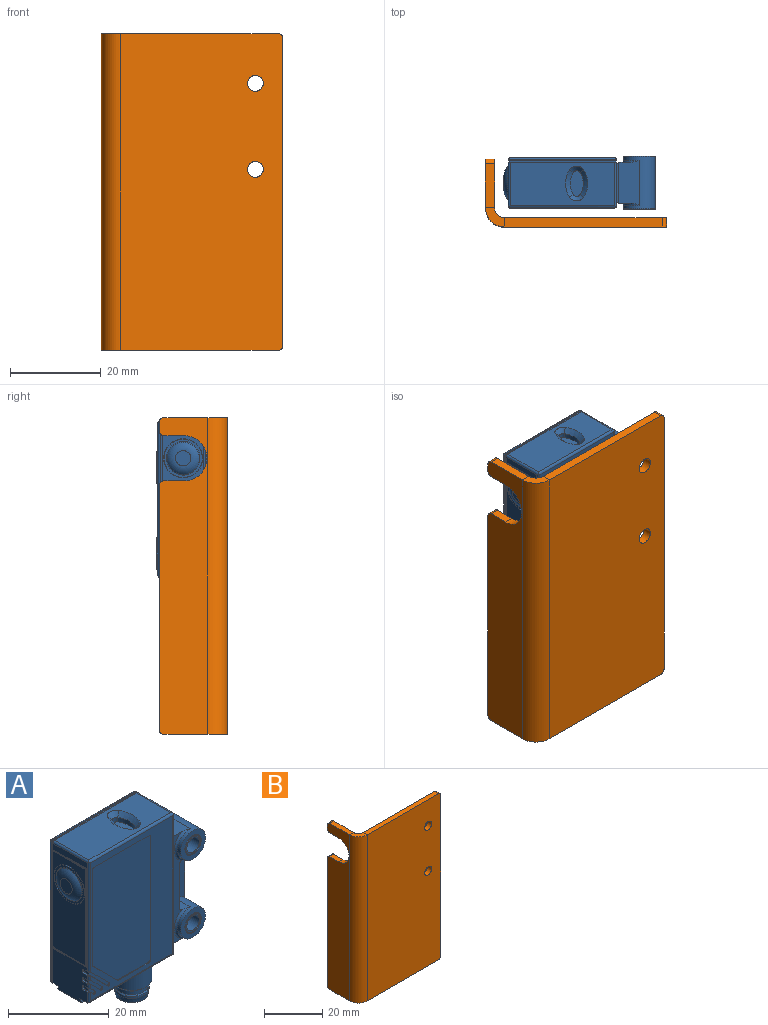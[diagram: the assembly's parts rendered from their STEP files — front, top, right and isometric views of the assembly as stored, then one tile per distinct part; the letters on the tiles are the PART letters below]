
ASSEMBLY  parts=2 mates=1
PART A: 180 faces, bbox 33.5x12.5x43.6 mm
  f0: cylinder r=4mm len=8mm, axis (0,0,-1), area 110.2mm2, adj f1,f8
  f1: cone r=3.69mm half-angle=45deg, axis (0,0,1), area 20.1mm2, adj f0,f179
  f2: cylinder r=3.25mm len=6.5mm, axis (0,0,-1), area 20.4mm2, adj f3,f179
  f3: cone r=3.35mm half-angle=38.7deg, axis (0,0,-1), area 6.7mm2, adj f2,f4
  f4: cylinder r=3.45mm len=6.9mm, axis (0,0,-1), area 10.8mm2, adj f3,f5
  f5: cone r=3.36mm half-angle=9.1deg, axis (0,0,1), area 23.1mm2, adj f4,f6
  f6: torus R=3.08mm, axis (0,0,1), area 5.7mm2, adj f5,f178
  f7: cylinder r=2.9mm len=5.8mm, axis (0,0,-1), area 91.1mm2, adj f177,f178
  f8: torus R=5mm, axis (0,0,1), area 40.8mm2, adj f0,f121,f170,f171
  f9: torus R=4mm, axis (0,-1,0), area 7.6mm2, adj f14,f98,f105,f107
  f10: torus R=4mm, axis (0,-1,0), area 7.6mm2, adj f13,f91,f101,f107
  f11: torus R=4mm, axis (0,-1,0), area 7.6mm2, adj f14,f100,f102,f105
  f12: torus R=4mm, axis (0,-1,0), area 7.6mm2, adj f13,f92,f101,f102
  f13: cylinder r=3.5mm len=11.6mm, axis (0,1,0), area 140.1mm2, adj f10,f12,f79,f84,f85,f87,f89,f90
  f14: cylinder r=3.5mm len=11.6mm, axis (0,1,0), area 140.1mm2, adj f9,f11,f82,f84,f85,f87,f89,f90
  f15: cone r=2.25mm half-angle=45deg, axis (0,-1,0), area 2mm2, adj f16,f82
  f16: cone r=2.12mm half-angle=56.3deg, axis (0,1,0), area 2.4mm2, adj f15,f83
  f17: cylinder r=1.75mm len=11.6mm, axis (0,1,0), area 127.5mm2, adj f81,f83
  f18: cone r=2.12mm half-angle=56.3deg, axis (0,-1,0), area 2.4mm2, adj f19,f81
  f19: cone r=2.25mm half-angle=45deg, axis (0,1,0), area 2mm2, adj f18,f104
  f20: cone r=2.25mm half-angle=45deg, axis (0,-1,0), area 2mm2, adj f21,f79
  f21: cone r=2.12mm half-angle=56.3deg, axis (0,1,0), area 2.4mm2, adj f20,f80
  f22: cylinder r=1.75mm len=11.6mm, axis (0,1,0), area 127.5mm2, adj f78,f80
  f23: cone r=2.12mm half-angle=56.3deg, axis (0,-1,0), area 2.4mm2, adj f24,f78
  f24: cone r=2.25mm half-angle=45deg, axis (0,1,0), area 2mm2, adj f23,f103
  f25: torus R=1.7mm, axis (-1,0,0), area 35.5mm2, adj f26,f53
  f26: torus R=3.71mm, axis (-1,0,0), area 3.8mm2, adj f25,f52
  f27: cylinder r=4.23mm len=8.45mm, axis (1,0,0), area 0.3mm2, adj f51,f52
  f28: cylinder r=4.3mm len=8.6mm, axis (1,0,0), area 118.9mm2, adj f50,f68
  f29: cylinder r=4.22mm len=8.45mm, axis (1,0,0), area 116.8mm2, adj f50,f51
  f30: plane 1.39x0.4mm, normal (0,0,1), area 0.5mm2, adj f34,f37,f48,f49
  f31: plane 1.39x0.4mm, normal (0,0,1), area 0.5mm2, adj f32,f39,f46,f49
  f32: plane 1.89x0.99mm, normal (-1,0,0), area 1.4mm2, adj f31,f38,f39,f43,f46,f136
  f33: plane 1.89x0.99mm, normal (-1,0,0), area 1.4mm2, adj f35,f40,f41,f44,f45,f138
  f34: plane 1.89x0.99mm, normal (-1,0,0), area 1.4mm2, adj f30,f36,f37,f42,f48,f146
  f35: plane 1.39x0.4mm, normal (0,0,1), area 0.5mm2, adj f33,f41,f45,f49
  f36: plane 1x0.4mm, normal (0,0,-1), area 0.4mm2, adj f34,f37,f47,f49,f154
  f37: cylinder r=0.49mm len=0.99mm, axis (-1,0,0), area 0.6mm2, adj f30,f34,f36,f49
  f38: plane 1x0.4mm, normal (0,0,-1), area 0.4mm2, adj f32,f39,f48,f49,f151
  f39: cylinder r=0.49mm len=0.99mm, axis (-1,0,0), area 0.6mm2, adj f31,f32,f38,f49
  f40: plane 1x0.4mm, normal (0,0,-1), area 0.4mm2, adj f33,f41,f46,f49,f137
  f41: cylinder r=0.49mm len=0.99mm, axis (-1,0,0), area 0.6mm2, adj f33,f35,f40,f49
  f42: plane 4.91x4.91mm, normal (0.71,0,0.71), area 2.8mm2, adj f34,f48,f146,f152,f172
  f43: plane 2.91x2.91mm, normal (0.71,0,0.71), area 1.6mm2, adj f32,f46,f136,f149,f172
  f44: plane 0.91x0.91mm, normal (0.71,0,0.71), area 0.5mm2, adj f33,f45,f138,f147,f172
  f45: cylinder r=0.5mm len=2.61mm, axis (0,0,-1), area 1.9mm2, adj f33,f35,f44,f49,f168,f172
  f46: cylinder r=0.5mm len=1.11mm, axis (0,0,-1), area 0.8mm2, adj f31,f32,f40,f43,f49,f137,f148,f172
  f47: cylinder r=0.5mm len=26.85mm, axis (0,0,-1), area 20.9mm2, adj f36,f49,f139,f140,f153,f154,f172
  f48: cylinder r=0.5mm len=1.11mm, axis (0,0,-1), area 0.8mm2, adj f30,f34,f38,f42,f49,f150,f151,f172
  f49: plane 34.82x9.6mm, normal (-1,0,0), area 99.8mm2, adj f30,f31,f35,f36,f37,f38,f39,f40
  f50: plane 8.6x8.6mm, normal (-1,0,0), area 2mm2, adj f28,f29
  f51: plane 8.45x8.45mm, normal (1,0,0), area 0mm2, adj f27,f29
  f52: plane 8.45x8.45mm, normal (-1,0,0), area 12.8mm2, adj f26,f27
  f53: plane 3.4x3.4mm, normal (-1,0,0), area 9.1mm2, adj f25
  f54: plane 9.3x0.2mm, normal (0,0,-1), area 1.9mm2, adj f49,f62,f67,f162
  f55: cylinder r=0.2mm len=0.2mm, axis (-1,0,0), area 0.1mm2, adj f56,f61,f68,f162
  f56: plane 8.8x0.2mm, normal (0,0,-1), area 1.8mm2, adj f55,f57,f68,f162
  f57: cylinder r=0.2mm len=0.2mm, axis (-1,0,0), area 0.1mm2, adj f56,f66,f68,f162
  f58: cylinder r=0.2mm len=0.2mm, axis (-1,0,0), area 0.1mm2, adj f59,f66,f68,f162
  f59: plane 8.8x0.2mm, normal (0,0,1), area 1.8mm2, adj f58,f60,f68,f162
  f60: cylinder r=0.2mm len=0.2mm, axis (-1,0,0), area 0.1mm2, adj f59,f61,f68,f162
  f61: plane 23x0.2mm, normal (0,-1,0), area 4.6mm2, adj f55,f60,f68,f162
  f62: cylinder r=0.2mm len=0.2mm, axis (-1,0,0), area 0.1mm2, adj f49,f54,f65,f162
  f63: plane 9.3x0.2mm, normal (0,0,1), area 1.9mm2, adj f49,f64,f67,f162
  f64: cylinder r=0.2mm len=0.2mm, axis (-1,0,0), area 0.1mm2, adj f49,f63,f65,f162
  f65: plane 23.6x0.2mm, normal (0,1,0), area 4.7mm2, adj f49,f62,f64,f162
  f66: plane 23x0.2mm, normal (0,1,0), area 4.6mm2, adj f57,f58,f68,f162
  f67: plane 34.5x24mm, normal (0,1,0), area 18.4mm2, adj f49,f54,f63,f121,f139,f141,f142,f155
  f68: plane 23.4x9.2mm, normal (-1,0,0), area 157.2mm2, adj f28,f55,f56,f57,f58,f59,f60,f61
  f69: cylinder r=0.88mm len=1.49mm, axis (0,0,1), area 2mm2, adj f70,f72,f73,f74
  f70: cylinder r=4.53mm len=4.88mm, axis (0,0,1), area 5.7mm2, adj f69,f71,f73,f77
  f71: cylinder r=0.88mm len=1.49mm, axis (0,0,1), area 2mm2, adj f70,f72,f73,f76
  f72: cylinder r=4.63mm len=4.85mm, axis (0,0,1), area 5.6mm2, adj f69,f71,f73,f75
  f73: plane 5.69x2.89mm, normal (0,0,1), area 12.7mm2, adj f69,f70,f71,f72
  f74: cone r=0.88mm half-angle=45deg, axis (0,0,1), area 3.9mm2, adj f69,f75,f77,f167
  f75: cone r=4.63mm half-angle=45deg, axis (0,0,1), area 8mm2, adj f72,f74,f76,f167
  f76: cone r=0.88mm half-angle=45deg, axis (0,0,1), area 3.9mm2, adj f71,f75,f77,f167
  f77: cone r=4.53mm half-angle=45deg, axis (0,0,1), area 8.1mm2, adj f70,f74,f76,f167
  f78: plane 4.1x4.1mm, normal (0,1,0), area 3.6mm2, adj f22,f23
  f79: plane 7x7mm, normal (0,-1,0), area 21.9mm2, adj f13,f20
  f80: plane 4.1x4.1mm, normal (0,-1,0), area 3.6mm2, adj f21,f22
  f81: plane 4.1x4.1mm, normal (0,1,0), area 3.6mm2, adj f17,f18
  f82: plane 7x7mm, normal (0,-1,0), area 21.9mm2, adj f14,f15
  f83: plane 4.1x4.1mm, normal (0,-1,0), area 3.6mm2, adj f16,f17
  f84: plane 15.39x0.5mm, normal (1,0,0), area 7.7mm2, adj f13,f14,f85,f90
  f85: cylinder r=0.5mm len=15.39mm, axis (0,0,-1), area 11.6mm2, adj f13,f14,f84,f87
  f86: cylinder r=0.5mm len=12mm, axis (0,0,-1), area 9mm2, adj f87,f93,f95,f97
  f87: plane 14.1x4.5mm, normal (0,-1,0), area 55.6mm2, adj f13,f14,f85,f86,f91,f98
  f88: cylinder r=0.5mm len=12mm, axis (0,0,-1), area 9mm2, adj f89,f94,f96,f99
  f89: plane 14.1x4.5mm, normal (0,1,0), area 55.6mm2, adj f13,f14,f88,f90,f92,f100
  f90: cylinder r=0.5mm len=15.39mm, axis (0,0,-1), area 11.6mm2, adj f13,f14,f84,f89
  f91: plane 4.34x2.14mm, normal (0,0,-1), area 7.8mm2, adj f10,f13,f87,f93,f107
  f92: plane 4.44x2.14mm, normal (0,0,-1), area 8mm2, adj f12,f13,f89,f94,f102
  f93: cylinder r=0.5mm len=3.7mm, axis (0,-1,0), area 2.7mm2, adj f86,f91,f95,f107
  f94: cylinder r=0.5mm len=3.8mm, axis (0,-1,0), area 2.8mm2, adj f88,f92,f96,f102
  f95: plane 11x3.2mm, normal (1,0,0), area 35.2mm2, adj f86,f93,f97,f107
  f96: plane 11x3.3mm, normal (1,0,0), area 36.3mm2, adj f88,f94,f99,f102
  f97: cylinder r=0.5mm len=3.7mm, axis (0,-1,0), area 2.7mm2, adj f86,f95,f98,f107
  f98: plane 4.34x2.14mm, normal (0,0,1), area 7.8mm2, adj f9,f14,f87,f97,f107
  f99: cylinder r=0.5mm len=3.8mm, axis (0,-1,0), area 2.8mm2, adj f88,f96,f100,f102
  f100: plane 4.44x2.14mm, normal (0,0,1), area 8mm2, adj f11,f14,f89,f99,f102
  f101: plane 10.14x4.69mm, normal (0,0,1), area 41.7mm2, adj f10,f12,f13,f102,f106,f107
  f102: plane 26x2.61mm, normal (0,1,0), area 40.8mm2, adj f11,f12,f92,f94,f96,f99,f100,f101
  f103: plane 7x7mm, normal (0,1,0), area 21.9mm2, adj f13,f24
  f104: plane 7x7mm, normal (0,1,0), area 21.9mm2, adj f14,f19
  f105: plane 10.14x4.69mm, normal (0,0,-1), area 41.7mm2, adj f9,f11,f14,f102,f106,f107
  f106: plane 26x9mm, normal (-1,0,0), area 13.8mm2, adj f101,f102,f105,f107,f108,f109,f110,f111
  f107: plane 26x2.61mm, normal (0,-1,0), area 40.8mm2, adj f9,f10,f91,f93,f95,f97,f98,f101
  f108: plane 25.6x0.45mm, normal (0,-1,0), area 11.5mm2, adj f106,f109,f111,f142
  f109: plane 8.6x0.45mm, normal (0,0,1), area 3.9mm2, adj f106,f108,f110,f142
  f110: plane 25.6x0.45mm, normal (0,1,0), area 11.5mm2, adj f106,f109,f111,f142
  f111: plane 8.6x0.45mm, normal (0,0,-1), area 3.9mm2, adj f106,f108,f110,f142
  f112: plane 3.8x1.64mm, normal (-0.45,0,-0.89), area 7mm2, adj f113,f114,f116,f119
  f113: plane 2.33x0.82mm, normal (0,-1,0), area 1.1mm2, adj f112,f114,f115,f119
  f114: plane 3.8x0.3mm, normal (0,0,-1), area 1.1mm2, adj f112,f113,f115,f116
  f115: plane 3.8x0.82mm, normal (0.91,0,-0.42), area 3.4mm2, adj f113,f114,f116,f119
  f116: plane 2.33x0.82mm, normal (0,1,0), area 1.1mm2, adj f112,f114,f115,f119
  f117: plane 11.9x0.82mm, normal (0,-0.88,0.47), area 11.1mm2, adj f49,f119,f120,f121
  f118: plane 11.9x0.82mm, normal (0,0.88,0.47), area 11.1mm2, adj f49,f119,f120,f121
  f119: plane 11.9x6.77mm, normal (0,0,-1), area 71.7mm2, adj f49,f112,f113,f115,f116,f117,f118,f120
  f120: plane 6.77x0.82mm, normal (1,0,0), area 5.2mm2, adj f117,f118,f119,f121
  f121: plane 23.5x9.6mm, normal (0,0,-1), area 79.1mm2, adj f8,f49,f67,f117,f118,f120,f164,f168
  f122: plane 6.92x6.92mm, normal (0.71,0,0.71), area 2mm2, adj f123,f131,f132,f172
  f123: cylinder r=0.3mm len=0.21mm, axis (0,-1,0), area 0mm2, adj f122,f124,f132,f172
  f124: plane 8.68x0.2mm, normal (0,0,1), area 1.7mm2, adj f123,f125,f132,f172
  f125: cylinder r=0.5mm len=0.5mm, axis (0,-1,0), area 0.2mm2, adj f124,f126,f132,f172
  f126: plane 29.9x0.2mm, normal (-1,0,0), area 6mm2, adj f125,f127,f132,f172
  f127: cylinder r=0.5mm len=0.5mm, axis (0,-1,0), area 0.2mm2, adj f126,f128,f132,f172
  f128: plane 15.4x0.2mm, normal (0,0,-1), area 3.1mm2, adj f127,f129,f132,f172
  f129: cylinder r=0.5mm len=0.5mm, axis (0,-1,0), area 0.2mm2, adj f128,f130,f132,f172
  f130: plane 23.18x0.2mm, normal (1,0,0), area 4.6mm2, adj f129,f131,f132,f172
  f131: cylinder r=0.3mm len=0.21mm, axis (0,-1,0), area 0mm2, adj f122,f130,f132,f172
  f132: plane 30.9x16.4mm, normal (0,-1,0), area 481.4mm2, adj f122,f123,f124,f125,f126,f127,f128,f129
  f133: cylinder r=0.5mm len=34.21mm, axis (0,0,-1), area 26.6mm2, adj f140,f141,f142,f164,f168,f172
  f134: cylinder r=0.5mm len=34.21mm, axis (0,0,-1), area 26.6mm2, adj f144,f145,f169,f174,f175,f176
  f135: cylinder r=0.5mm len=34.35mm, axis (0,0,-1), area 26.6mm2, adj f143,f145,f166,f169,f174
  f136: plane 3.99x3.5mm, normal (0,-1,0), area 3.3mm2, adj f32,f43,f149,f150,f151
  f137: plane 0.4x0.39mm, normal (0,0,-1), area 0.1mm2, adj f40,f46,f138,f148
  f138: plane 1.99x1.5mm, normal (0,-1,0), area 1.3mm2, adj f33,f44,f137,f147,f148
  f139: cylinder r=0.5mm len=9.95mm, axis (0,1,0), area 7.7mm2, adj f47,f49,f67,f140,f167
  f140: cylinder r=0.5mm len=23.71mm, axis (-1,0,0), area 18.3mm2, adj f47,f133,f139,f141,f167,f172
  f141: cylinder r=0.5mm len=9.95mm, axis (0,1,0), area 7.7mm2, adj f67,f133,f140,f142,f167
  f142: plane 33.5x9.6mm, normal (1,0,0), area 101.4mm2, adj f67,f108,f109,f110,f111,f133,f141,f164
  f143: plane 34x0.1mm, normal (-1,0,0), area 3.4mm2, adj f135,f163,f165,f166
  f144: cylinder r=0.5mm len=0.5mm, axis (0,1,0), area 0.2mm2, adj f134,f163,f169,f173,f175
  f145: cylinder r=0.5mm len=23.85mm, axis (-1,0,0), area 18.4mm2, adj f134,f135,f165,f174,f176
  f146: plane 5.99x5.5mm, normal (0,-1,0), area 5.3mm2, adj f34,f42,f152,f153,f154
  f147: cylinder r=0.35mm len=0.6mm, axis (0,-1,0), area 0.4mm2, adj f44,f138,f148,f172
  f148: plane 1.39x1.39mm, normal (-0.71,0,-0.71), area 0.8mm2, adj f46,f137,f138,f147,f172
  f149: cylinder r=0.35mm len=0.6mm, axis (0,-1,0), area 0.4mm2, adj f43,f136,f150,f172
  f150: plane 3.39x3.39mm, normal (-0.71,0,-0.71), area 1.9mm2, adj f48,f136,f149,f151,f172
  f151: plane 0.4x0.39mm, normal (0,0,-1), area 0.1mm2, adj f38,f48,f136,f150
  f152: cylinder r=0.35mm len=0.6mm, axis (0,-1,0), area 0.4mm2, adj f42,f146,f153,f172
  f153: plane 5.39x5.39mm, normal (-0.71,0,-0.71), area 3.1mm2, adj f47,f146,f152,f154,f172
  f154: plane 0.4x0.39mm, normal (0,0,-1), area 0.1mm2, adj f36,f47,f146,f153
  f155: cylinder r=0.3mm len=0.4mm, axis (0,-1,0), area 0.2mm2, adj f67,f156,f162,f163
  f156: plane 23x0.4mm, normal (0,0,1), area 9.2mm2, adj f67,f155,f157,f163
  f157: cylinder r=0.3mm len=0.4mm, axis (0,-1,0), area 0.2mm2, adj f67,f156,f158,f163
  f158: plane 33.5x0.4mm, normal (1,0,0), area 13.4mm2, adj f67,f157,f159,f163
  f159: cylinder r=0.3mm len=0.4mm, axis (0,-1,0), area 0.2mm2, adj f67,f158,f160,f163
  f160: plane 23x0.4mm, normal (0,0,-1), area 9.2mm2, adj f67,f159,f161,f163
  f161: cylinder r=0.3mm len=0.4mm, axis (0,-1,0), area 0.2mm2, adj f67,f160,f162,f163
  f162: plane 33.5x9.9mm, normal (-1,0,0), area 26.1mm2, adj f54,f55,f56,f57,f58,f59,f60,f61
  f163: plane 34.5x24mm, normal (0,-1,0), area 23.2mm2, adj f143,f144,f155,f156,f157,f158,f159,f160
  f164: cylinder r=0.5mm len=9.95mm, axis (0,1,0), area 7.7mm2, adj f67,f121,f133,f142,f168
  f165: plane 23.5x0.1mm, normal (0,0,-1), area 2.4mm2, adj f143,f145,f163,f176
  f166: cylinder r=0.5mm len=0.5mm, axis (0,1,0), area 0.2mm2, adj f135,f143,f163,f169,f173
  f167: plane 23x9.6mm, normal (0,0,1), area 191.1mm2, adj f67,f74,f75,f76,f77,f139,f140,f141
  f168: cylinder r=0.5mm len=23.85mm, axis (-1,0,0), area 18.4mm2, adj f45,f121,f133,f164,f172
  f169: cylinder r=0.5mm len=23.71mm, axis (-1,0,0), area 18.3mm2, adj f134,f135,f144,f166,f173,f174
  f170: cylinder r=2mm len=3.92mm, axis (-1,0,0), area 0.4mm2, adj f8,f121
  f171: cylinder r=2mm len=3.92mm, axis (-1,0,0), area 0.4mm2, adj f8,f121
  f172: plane 33.5x23mm, normal (0,-1,0), area 279.5mm2, adj f42,f43,f44,f45,f46,f47,f48,f122
  f173: plane 23x0.1mm, normal (0,0,1), area 2.3mm2, adj f144,f163,f166,f169
  f174: plane 33.5x23mm, normal (0,1,0), area 770.5mm2, adj f134,f135,f145,f169
  f175: plane 33.5x0.1mm, normal (1,0,0), area 3.4mm2, adj f134,f144,f163,f176
  f176: cylinder r=0.5mm len=0.5mm, axis (0,1,0), area 0.2mm2, adj f134,f145,f163,f165,f175
  f177: plane 5.8x5.8mm, normal (0,0,-1), area 26.4mm2, adj f7
  f178: plane 6.16x6.16mm, normal (0,0,-1), area 3.4mm2, adj f6,f7
  f179: plane 6.77x6.77mm, normal (0,0,-1), area 2.8mm2, adj f1,f2
PART B: 26 faces, bbox 40x15x70 mm
  f0: plane 34.7x2mm, normal (0,0,1), area 69.4mm2, adj f5,f6,f8,f23
  f1: plane 68x2mm, normal (1,0,0), area 136mm2, adj f5,f6,f7,f8
  f2: cylinder r=1.75mm len=3.5mm, axis (0,-1,0), area 22mm2, adj f5,f6
  f3: cylinder r=1.75mm len=3.5mm, axis (0,-1,0), area 22mm2, adj f5,f6
  f4: plane 34.7x2mm, normal (0,0,-1), area 69.4mm2, adj f5,f6,f7,f22
  f5: plane 70x35.7mm, normal (0,1,0), area 2479.3mm2, adj f0,f1,f2,f3,f4,f7,f8,f25
  f6: plane 70x35.7mm, normal (0,-1,0), area 2479.3mm2, adj f0,f1,f2,f3,f4,f7,f8,f24
  f7: cylinder r=1mm len=2mm, axis (0,-1,0), area 3.1mm2, adj f1,f4,f5,f6
  f8: cylinder r=1mm len=2mm, axis (0,-1,0), area 3.1mm2, adj f0,f1,f5,f6
  f9: plane 2x2mm, normal (0,1,0), area 4mm2, adj f16,f17,f19,f21
  f10: plane 9.7x2mm, normal (0,0,1), area 19.4mm2, adj f16,f17,f21,f23
  f11: plane 9.7x2mm, normal (0,0,-1), area 19.4mm2, adj f16,f17,f18,f22
  f12: plane 54x2mm, normal (0,1,0), area 108mm2, adj f16,f17,f18,f20
  f13: plane 4.5x2mm, normal (0,0,1), area 9mm2, adj f14,f16,f17,f20
  f14: cylinder r=5mm len=10mm, axis (1,0,0), area 31.4mm2, adj f13,f15,f16,f17
  f15: plane 4.5x2mm, normal (0,0,-1), area 9mm2, adj f14,f16,f17,f19
  f16: plane 70x10.7mm, normal (1,0,0), area 653.9mm2, adj f9,f10,f11,f12,f13,f14,f15,f18
  f17: plane 70x10.7mm, normal (-1,0,0), area 653.9mm2, adj f9,f10,f11,f12,f13,f14,f15,f18
  f18: cylinder r=1mm len=2mm, axis (1,0,0), area 3.1mm2, adj f11,f12,f16,f17
  f19: cylinder r=1mm len=2mm, axis (-1,0,0), area 3.1mm2, adj f9,f15,f16,f17
  f20: cylinder r=1mm len=2mm, axis (1,0,0), area 3.1mm2, adj f12,f13,f16,f17
  f21: cylinder r=1mm len=2mm, axis (1,0,0), area 3.1mm2, adj f9,f10,f16,f17
  f22: plane 4.3x4.3mm, normal (0,0,-1), area 10.4mm2, adj f4,f11,f24,f25
  f23: plane 4.3x4.3mm, normal (0,0,1), area 10.4mm2, adj f0,f10,f24,f25
  f24: cylinder r=4.3mm len=70mm, axis (0,0,-1), area 472.8mm2, adj f6,f17,f22,f23
  f25: cylinder r=2.3mm len=70mm, axis (0,0,-1), area 252.9mm2, adj f5,f16,f22,f23
PLACE A t=(-22.12,-20.75,12.85)mm
PLACE B t=(-22.12,-21,12.85)mm
MATE pin_slot A.f9 <-> B.f3  axis (0,-1,0) through (-10.62,-26.5,27.15)mm
